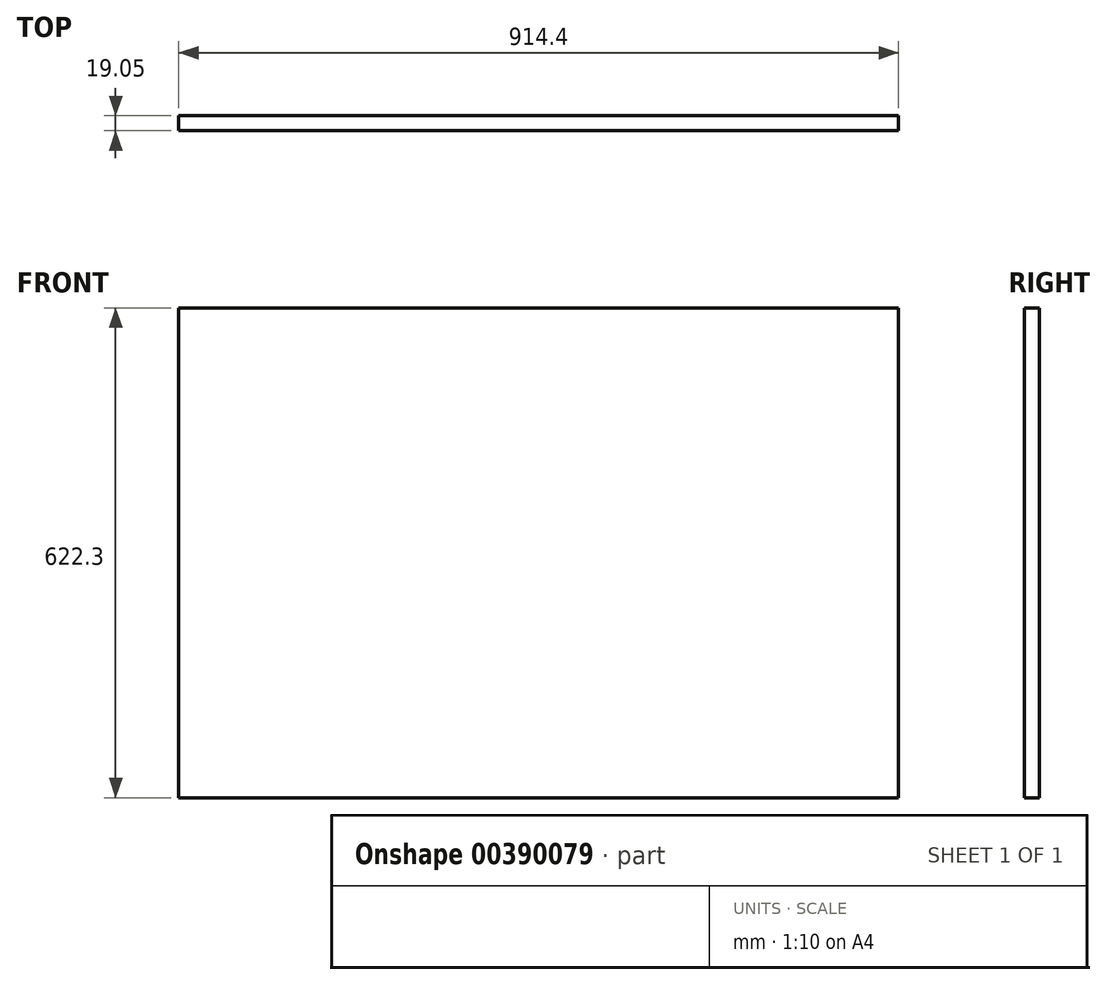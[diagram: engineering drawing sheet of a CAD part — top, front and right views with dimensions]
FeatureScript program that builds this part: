
annotation { "Feature Type Name" : "Feature", "Feature Type Description" : "" }
export const myFeature = defineFeature(function(context is Context, id is Id, definition is map)
    precondition{}
    {
        {
            var Q0;
            Q0=qCreatedBy(makeId("Front.planeOp"),FACE);
            var sketch = newSketch(context, id + "F0", { "sketchPlane" : qUnion([Q0])});
            skLineSegment(sketch, "E0.bottom", {"start": v(0, 0) * mm, "end": v(914.4, 0) * mm});
            skLineSegment(sketch, "E0.top", {"start": v(0, 622.3) * mm, "end": v(914.4, 622.3) * mm});
            skLineSegment(sketch, "E0.left", {"start": v(0, 0) * mm, "end": v(0, 622.3) * mm});
            skLineSegment(sketch, "E0.right", {"start": v(914.4, 0) * mm, "end": v(914.4, 622.3) * mm});
            skSolve(sketch);
        }
        {
            var Q0;
            Q0 = qSketchRegion(id + "F0", true);
            var Q1;
            Q1=makeQuery(id+"F0.imprint","IMPRINT",FACE,{"disambiguationData":[TD([[makeQuery(id+"F0.imprint","IMPRINT",EDGE,{"derivedFrom":sQuery(id+"F0.wireOp",EDGE,"E0.bottom")}),1.0]])]});
            extrude(context, id + "F1", {"entities" : qUnion([Q0, Q1]), "depth" : 19.05 * mm});
        }
    });
